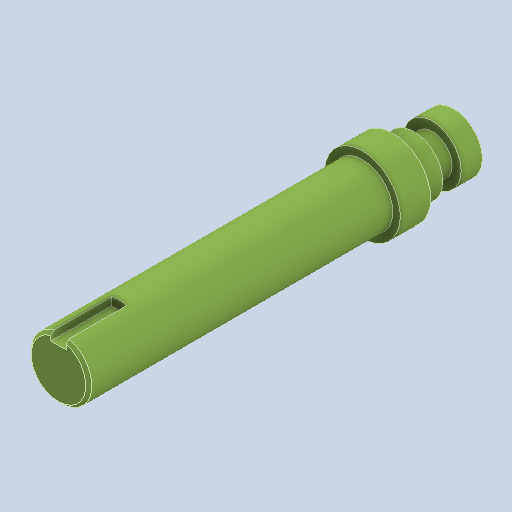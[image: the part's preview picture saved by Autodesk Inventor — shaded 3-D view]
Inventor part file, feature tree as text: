
AUTODESK INVENTOR PART (.ipt)
format: ipt  version: 2022 (Build 260153000, 153)  size: 142,336 bytes
history: native  units: in
note: dims shown in document units (in); Inventor stores cm internally (conversion verified against a paired STEP export)
features: extrude x6, sketch x6, chamfer x1
ambient origin geometry x8: Origin, YZ Plane, XZ Plane, XY Plane, X Axis, Y Axis, Z Axis, Center Point
bodies: Solid1 (feature_tree)
feature tree (13):
  extrude  "Extrusion1"  Depth=0.2756in TaperAngle=0.0deg
  extrude  "Extrusion2"  Depth=0.2362in TaperAngle=0.0deg
  extrude  "Extrusion3"  Depth=0.2756in TaperAngle=0.0deg
  extrude  "Extrusion4"  Depth=0.3937in TaperAngle=0.0deg
  extrude  "Extrusion5"  Depth=0.7874in TaperAngle=0.0deg
  chamfer  "Chamfer1"  Distance=0.0394in Angle=45.0deg
  extrude  "Extrusion6"  Depth=0.1969in
  sketch  "Sketch1"  dims[d0=0.748in d1=0.2756in d2=0.0in]
  sketch  "Sketch2"  dims[d3=0.5118in d4=0.2362in d5=0.0in]
  sketch  "Sketch3"  dims[d6=0.748in d7=0.2756in d8=0.0in]
  sketch  "Sketch4"  dims[d9=0.9843in d10=0.3937in d11=0.0in]
  sketch  "Sketch5"  dims[d12=0.7874in d13=3.937in d14=0.0in d15=0.0394in d16=0.0787in d17=45.0deg]
  sketch  "Sketch6"  dims[d18=0.1969in d19=0.1969in d20=0.2756in d21=0.7874in d22=0.0in]
